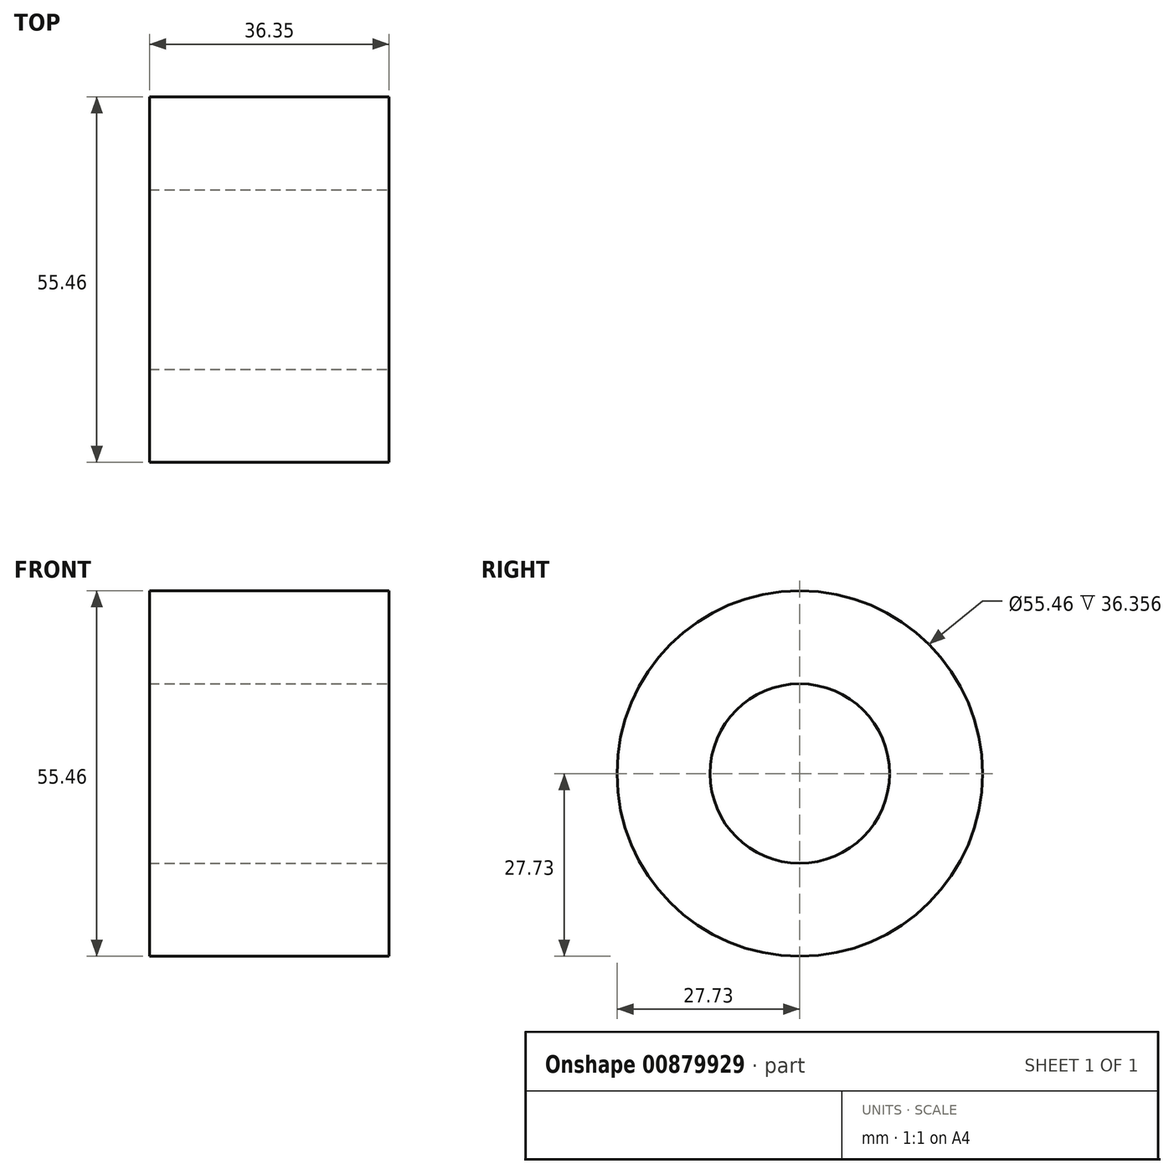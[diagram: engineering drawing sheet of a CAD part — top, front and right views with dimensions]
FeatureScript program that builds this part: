
annotation { "Feature Type Name" : "Feature", "Feature Type Description" : "" }
export const myFeature = defineFeature(function(context is Context, id is Id, definition is map)
    precondition{}
    {
        {
            var Q0;
            Q0=qCreatedBy(makeId("Front.planeOp"),FACE);
            var sketch = newSketch(context, id + "F0", { "sketchPlane" : qUnion([Q0])});
            skLineSegment(sketch, "E0", {"start": v(-114.93, 0) * mm, "end": v(67.28, 0) * mm, "construction": true});
            skLineSegment(sketch, "E1", {"start": v(-16.06, 13.61) * mm, "end": v(-16.06, 27.73) * mm});
            skLineSegment(sketch, "E2", {"start": v(-16.06, 27.73) * mm, "end": v(20.3, 27.73) * mm});
            skLineSegment(sketch, "E3", {"start": v(20.3, 27.73) * mm, "end": v(20.3, 13.61) * mm});
            skLineSegment(sketch, "E4", {"start": v(20.3, 13.61) * mm, "end": v(-16.06, 13.61) * mm});
            skSolve(sketch);
        }
        {
            var Q0;
            Q0=sQuery(id+"F0.wireOp",EDGE,"E2");
            var Q1;
            Q1=sQuery(id+"F0.wireOp",EDGE,"E3");
            var Q2;
            Q2=sQuery(id+"F0.wireOp",EDGE,"E1");
            var Q3;
            Q3=sQuery(id+"F0.wireOp",EDGE,"E4");
            var Q4;
            Q4=sQuery(id+"F0.wireOp",EDGE,"E0");
            revolve(context, id + "F1", {"bodyType" : ToolBodyType.SURFACE, "surfaceOperationType" : NewSurfaceOperationType.NEW, "surfaceEntities" : qUnion([Q0, Q1, Q2, Q3]), "axis" : qUnion([Q4]), "revolveType" : RevolveType.FULL});
        }
    });
